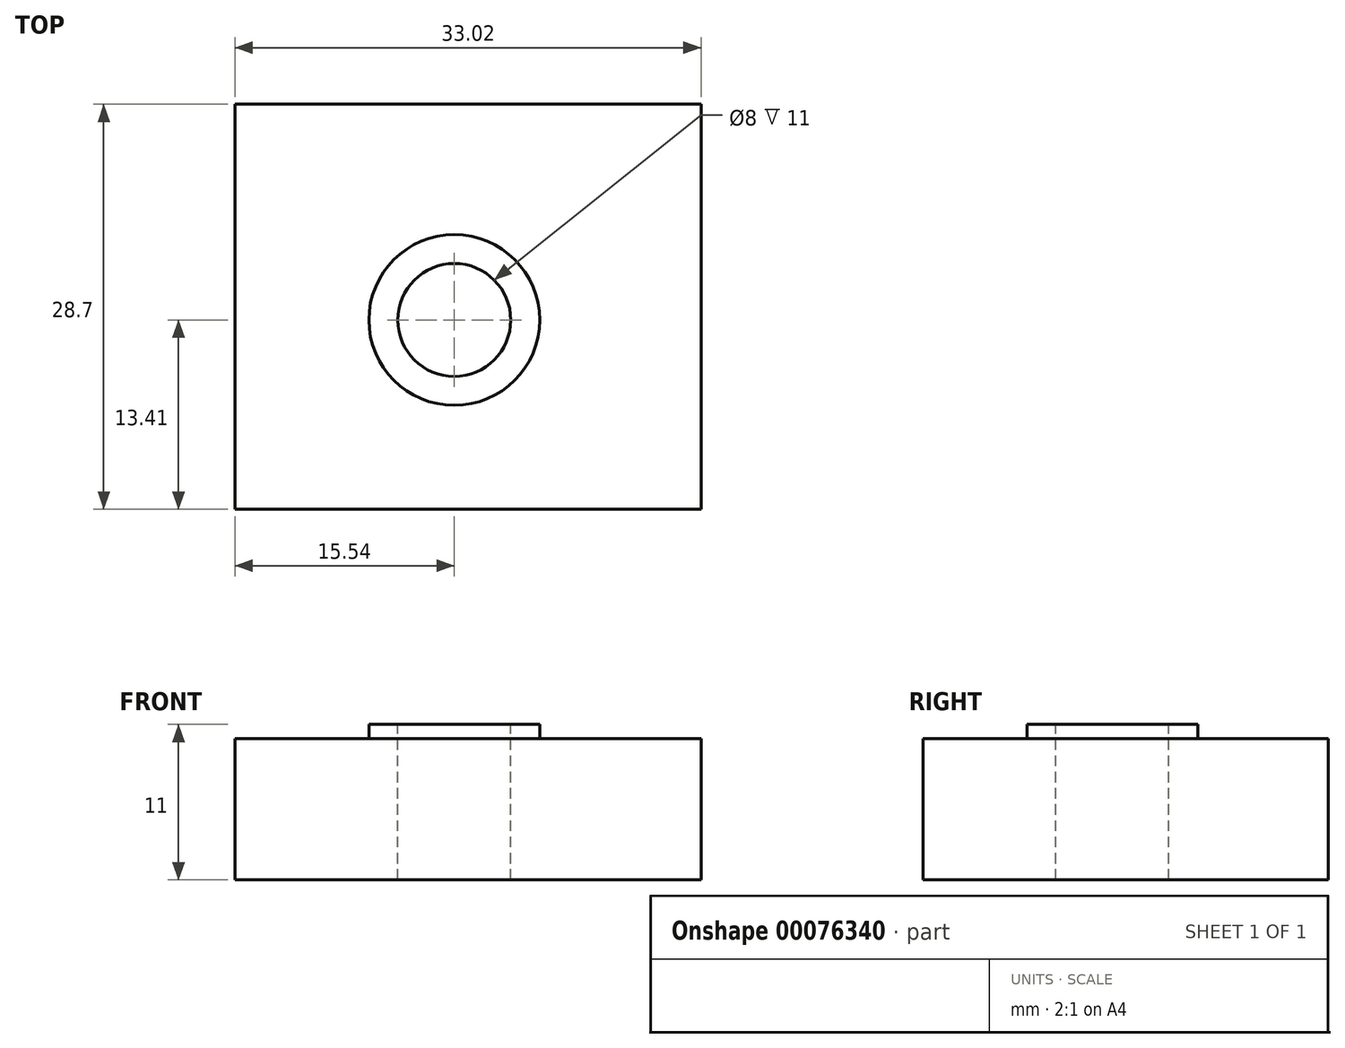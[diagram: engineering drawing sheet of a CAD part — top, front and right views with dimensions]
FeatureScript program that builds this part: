
annotation { "Feature Type Name" : "Feature", "Feature Type Description" : "" }
export const myFeature = defineFeature(function(context is Context, id is Id, definition is map)
    precondition{}
    {
        {
            var Q0;
            Q0=qCreatedBy(makeId("Top.planeOp"),FACE);
            var sketch = newSketch(context, id + "F0", { "sketchPlane" : qUnion([Q0])});
            skCircle(sketch, "E0.0", {"center": v(0, 0) * mm, "radius": 6.05 * mm});
            skCircle(sketch, "E1.0", {"center": v(0, 0) * mm, "radius": 4 * mm});
            skLineSegment(sketch, "E2.bottom", {"start": v(-19.45, -18.3) * mm, "end": v(17.64, -18.3) * mm});
            skLineSegment(sketch, "E2.top", {"start": v(-19.45, 15.13) * mm, "end": v(17.64, 15.13) * mm});
            skLineSegment(sketch, "E2.left", {"start": v(-19.45, -18.3) * mm, "end": v(-19.45, 15.13) * mm});
            skLineSegment(sketch, "E2.right", {"start": v(17.64, -18.3) * mm, "end": v(17.64, 15.13) * mm});
            skSolve(sketch);
        }
        {
            var Q0;
            Q0=makeQuery(id+"F0.imprint","IMPRINT",FACE,{"disambiguationData":[TD([[makeQuery(id+"F0.imprint","IMPRINT",EDGE,{"derivedFrom":sQuery(id+"F0.wireOp",EDGE,"E0.0")}),1.0]])]});
            extrude(context, id + "F1", {"entities" : qUnion([Q0]), "oppositeDirection" : true, "depth" : 1 * mm});
        }
        {
            var Q0;
            Q0=makeQuery(id+"F1.opExtrude","CAP_FACE",FACE,{"disambiguationData":[OSD([sQuery(id+"F0.wireOp",EDGE,"E0.0"),sQuery(id+"F0.wireOp",EDGE,"E1.0")])],"isStart":false});
            var sketch = newSketch(context, id + "F2", { "sketchPlane" : qUnion([Q0])});
            skLineSegment(sketch, "E3.bottom", {"start": v(-15.54, 13.41) * mm, "end": v(17.48, 13.41) * mm});
            skLineSegment(sketch, "E3.top", {"start": v(-15.54, -15.29) * mm, "end": v(17.48, -15.29) * mm});
            skLineSegment(sketch, "E3.left", {"start": v(-15.54, 13.41) * mm, "end": v(-15.54, -15.29) * mm});
            skLineSegment(sketch, "E3.right", {"start": v(17.48, 13.41) * mm, "end": v(17.48, -15.29) * mm});
            skCircle(sketch, "E4.0", {"center": v(0, 0) * mm, "radius": 4 * mm});
            skSolve(sketch);
        }
        {
            var Q0;
            Q0 = qSketchRegion(id + "F2", true);
            extrude(context, id + "F3", {"entities" : qUnion([Q0]), "operationType" : NewBodyOperationType.ADD, "depth" : 10 * mm});
        }
    });
